# Revit family: VENTS-VKH
name_source: partatom
category: Mechanical Equipment
units: mm (PartAtom-declared; Revit-internal decimal feet)

## family parameters
Always vertical = Yes
Classification = None
Cut with Voids When Loaded = No
OmniClass Number = 23.75.35.17.14
OmniClass Title = Fans, Single Units
Part Type = Normal
Room Calculation Point = No
Round Connector Dimension = Use Diameter
Shared = No
Work Plane-Based = No

## types (38) — shared parameters
Casing Material = Fan Zinc
Description = Centrifugal roof fan with horizontal air discharge
Family Version = 1.0
Grid Material = Grid Cross Zinc
Hb = 30 mm  [stored 0.0984252 ft]
Load Classification = HVAC
Maintenance Zone Front Depth = 400 mm
Maintenance Zone Material = Maintenance Zone
Maintenance Zone Side Depth = 400 mm
Manufacturer = Vents
Power Factor = 1
Protection rating = IP X4
URL = https://ventilation-system.com
grGap1 = 1 mm  [stored 0.00328084 ft]
grGap2 = 20 mm  [stored 0.0656168 ft]
zero-valued in all types: Sound Pressure Level at 1 m (dBA), Sound Pressure Level at 3 m (dBA)

## per-type parameters (varying)
| type | A | Ac | Atop | B | C | Current | D | Duct Connection Size | H | Hc | Ht1 | Ht2 | Maximum Air Flow | Model | Noise Level at 3 m (dBa) | Number of Poles | RPM (min-1) | Transported Air Temperature (°C) | Type Comments | Voltage | Weight | gsA |
| VKH 2E 190 (50Hz) | 351 mm | 298 mm  [stored 0.97769 ft] | 294 mm  [stored 0.964567 ft] | 350 mm | 245 mm  [stored 0.803806 ft] | 0 A | 213 mm  [stored 0.698819 ft] | 180 mm  [stored 0.590551 ft] | 189 mm  [stored 0.620079 ft] | 78 mm | 59 mm | 22 mm  [stored 0.0721785 ft] | 610 m³/h | VKH 2E 190 | 48 | 1 | 2680 | -25...+50 | Centrifugal roof fan VKH 2E 190 | 230 V | 8.20 kg | 281 mm |
| VKH 2E 190 (60Hz) | 351 mm | 298 mm  [stored 0.97769 ft] | 294 mm  [stored 0.964567 ft] | 350 mm | 245 mm  [stored 0.803806 ft] | 0 A | 213 mm  [stored 0.698819 ft] | 180 mm  [stored 0.590551 ft] | 189 mm  [stored 0.620079 ft] | 78 mm | 59 mm | 22 mm  [stored 0.0721785 ft] | 654 m³/h | VKH 2E 190 | 49 | 1 | 2980 | -25...+50 | Centrifugal roof fan VKH 2E 190 | 230 V | 8.20 kg | 281 mm |
| VKH 2E 220 (50Hz) | 337 mm | 284 mm  [stored 0.931759 ft] | 292 mm  [stored 0.958005 ft] | 338 mm | 245 mm  [stored 0.803806 ft] | 0 A | 213 mm  [stored 0.698819 ft] | 180 mm  [stored 0.590551 ft] | 180 mm  [stored 0.590551 ft] | 75 mm | 46 mm  [stored 0.150919 ft] | 29 mm  [stored 0.0951444 ft] | 880 m³/h | VKH 2E 220 | 50 | 1 | 2580 | -25...+50 | Centrifugal roof fan VKH 2E 220 | 230 V | 7.00 kg | 270 mm |
| VKH 2E 220 (60Hz) | 337 mm | 284 mm  [stored 0.931759 ft] | 292 mm  [stored 0.958005 ft] | 338 mm | 245 mm  [stored 0.803806 ft] | 1 A | 213 mm  [stored 0.698819 ft] | 180 mm  [stored 0.590551 ft] | 180 mm  [stored 0.590551 ft] | 75 mm | 46 mm  [stored 0.150919 ft] | 29 mm  [stored 0.0951444 ft] | 883 m³/h | VKH 2E 220 | 51 | 1 | 2840 | -25...+50 | Centrifugal roof fan VKH 2E 220 | 230 V | 7.00 kg | 270 mm |
| VKH 2E 225 (50Hz) | 351 mm | 298 mm  [stored 0.97769 ft] | 295 mm  [stored 0.967848 ft] | 350 mm | 245 mm  [stored 0.803806 ft] | 1 A | 210 mm  [stored 0.688976 ft] | 180 mm  [stored 0.590551 ft] | 210 mm  [stored 0.688976 ft] | 99 mm | 59 mm | 22 mm  [stored 0.0721785 ft] | 915 m³/h | VKH 2E 225 | 51 | 1 | 2790 | -25...+50 | Centrifugal roof fan VKH 2E 225 | 230 V | 9.20 kg | 281 mm |
| VKH 2E 225 (60Hz) | 351 mm | 298 mm  [stored 0.97769 ft] | 295 mm  [stored 0.967848 ft] | 350 mm | 245 mm  [stored 0.803806 ft] | 1 A | 210 mm  [stored 0.688976 ft] | 180 mm  [stored 0.590551 ft] | 210 mm  [stored 0.688976 ft] | 99 mm | 59 mm | 22 mm  [stored 0.0721785 ft] | 1010 m³/h | VKH 2E 225 | 52 | 1 | 2820 | -25...+50 | Centrifugal roof fan VKH 2E 225 | 230 V | 9.20 kg | 281 mm |
| VKH 4E 225 (50Hz) | 351 mm | 298 mm  [stored 0.97769 ft] | 295 mm  [stored 0.967848 ft] | 350 mm | 245 mm  [stored 0.803806 ft] | 0 A | 210 mm  [stored 0.688976 ft] | 180 mm  [stored 0.590551 ft] | 233 mm  [stored 0.764436 ft] | 122 mm | 59 mm | 22 mm  [stored 0.0721785 ft] | 738 m³/h | VKH 4E 225 | 45 | 1 | 1400 | -25...+50 | Centrifugal roof fan VKH 4E 225 | 230 V | 8.80 kg | 281 mm |
| VKH 2E 250 (50Hz) | 451 mm | 398 mm | 394 mm | 450 mm | 330 mm | 1 A | 285 mm  [stored 0.935039 ft] | 250 mm  [stored 0.82021 ft] | 237 mm  [stored 0.777559 ft] | 126 mm  [stored 0.413386 ft] | 59 mm | 22 mm  [stored 0.0721785 ft] | 1450 m³/h | VKH 2E 250 | 54 | 1 | 2480 | -25...+50 | Centrifugal roof fan VKH 2E 250 | 230 V | 12.70 kg | 361 mm |
| VKH 2E 250 (60Hz) | 451 mm | 398 mm | 394 mm | 450 mm | 330 mm | 1 A | 285 mm  [stored 0.935039 ft] | 250 mm  [stored 0.82021 ft] | 237 mm  [stored 0.777559 ft] | 126 mm  [stored 0.413386 ft] | 59 mm | 22 mm  [stored 0.0721785 ft] | 1320 m³/h | VKH 2E 250 | 53 | 1 | 2320 | -25...+50 | Centrifugal roof fan VKH 2E 250 | 230 V | 12.70 kg | 361 mm |
| VKH 4E 250 (50Hz) | 451 mm | 398 mm | 394 mm | 450 mm | 330 mm | 0 A | 285 mm  [stored 0.935039 ft] | 250 mm  [stored 0.82021 ft] | 237 mm  [stored 0.777559 ft] | 126 mm  [stored 0.413386 ft] | 59 mm | 22 mm  [stored 0.0721785 ft] | 820 m³/h | VKH 4E 250 | 46 | 1 | 1440 | -25...+50 | Centrifugal roof fan VKH 4E 250 | 230 V | 12.10 kg | 361 mm |
| VKH 4E 280 (50Hz) | 451 mm | 398 mm | 394 mm | 450 mm | 330 mm | 1 A | 291 mm  [stored 0.954724 ft] | 250 mm  [stored 0.82021 ft] | 265 mm  [stored 0.869423 ft] | 154 mm | 59 mm | 22 mm  [stored 0.0721785 ft] | 1490 m³/h | VKH 4E 280 | 46 | 1 | 1446 | -25...+50 | Centrifugal roof fan VKH 4E 280 | 230 V | 13.50 kg | 361 mm |
| VKH 4E 280 (60Hz) | 451 mm | 398 mm | 394 mm | 450 mm | 330 mm | 1 A | 291 mm  [stored 0.954724 ft] | 250 mm  [stored 0.82021 ft] | 265 mm  [stored 0.869423 ft] | 154 mm | 59 mm | 22 mm  [stored 0.0721785 ft] | 1520 m³/h | VKH 4E 280 | 46 | 1 | 1710 | -25...+50 | Centrifugal roof fan VKH 4E 280 | 230 V | 13.50 kg | 361 mm |
| VKH 2E 310 (50Hz) | 451 mm | 398 mm | 394 mm | 450 mm | 330 mm | 1 A | 291 mm  [stored 0.954724 ft] | 250 mm  [stored 0.82021 ft] | 251 mm  [stored 0.823491 ft] | 140 mm  [stored 0.459318 ft] | 59 mm | 22 mm  [stored 0.0721785 ft] | 2150 m³/h | VKH 2E 310 | 58 | 1 | 2620 | -25...+50 | Centrifugal roof fan VKH 2E 310 | 230 V | 13.20 kg | 361 mm |
| VKH 4E 310 (50Hz) | 451 mm | 398 mm | 394 mm | 450 mm | 330 mm | 1 A | 285 mm  [stored 0.935039 ft] | 250 mm  [stored 0.82021 ft] | 287 mm  [stored 0.941601 ft] | 176 mm  [stored 0.577428 ft] | 59 mm | 22 mm  [stored 0.0721785 ft] | 2265 m³/h | VKH 4E 310 | 47 | 1 | 1420 | -25...+50 | Centrifugal roof fan VKH 4E 310 | 230 V | 14.20 kg | 361 mm |
| VKH 4E 310 (60Hz) | 451 mm | 398 mm | 394 mm | 450 mm | 330 mm | 1 A | 285 mm  [stored 0.935039 ft] | 250 mm  [stored 0.82021 ft] | 287 mm  [stored 0.941601 ft] | 176 mm  [stored 0.577428 ft] | 59 mm | 22 mm  [stored 0.0721785 ft] | 2425 m³/h | VKH 4E 310 | 49 | 1 | 1740 | -25...+50 | Centrifugal roof fan VKH 4E 310 | 230 V | 14.20 kg | 361 mm |
| VKH 4D 310 (50Hz) | 451 mm | 398 mm | 394 mm | 450 mm | 330 mm | 0 A | 285 mm  [stored 0.935039 ft] | 250 mm  [stored 0.82021 ft] | 287 mm  [stored 0.941601 ft] | 176 mm  [stored 0.577428 ft] | 59 mm | 22 mm  [stored 0.0721785 ft] | 2300 m³/h | VKH 4D 310 | 47 | 3 | 1410 | -25...+50 | Centrifugal roof fan VKH 4D 310 | 400 V | 14.20 kg | 361 mm |
| VKH 4D 310 (60Hz) | 451 mm | 398 mm | 394 mm | 450 mm | 330 mm | 0 A | 285 mm  [stored 0.935039 ft] | 250 mm  [stored 0.82021 ft] | 287 mm  [stored 0.941601 ft] | 176 mm  [stored 0.577428 ft] | 59 mm | 22 mm  [stored 0.0721785 ft] | 2442 m³/h | VKH 4D 310 | 48 | 3 | 1550 | -25...+50 | Centrifugal roof fan VKH 4D 310 | 400 V | 14.20 kg | 361 mm |
| VKH 4E 355 (50Hz) | 625 mm | 568 mm | 534 mm | 620 mm | 450 mm | 1 A | 438 mm | 400 mm | 322 mm | 176 mm  [stored 0.577428 ft] | 94 mm  [stored 0.308399 ft] | 22 mm  [stored 0.0721785 ft] | 2480 m³/h | VKH 4E 355 | 51 | 1 | 1420 | -30...+60 | Centrifugal roof fan VKH 4E 355 | 230 V | 28.30 kg | 500 mm |
| VKH 4E 355 (60Hz) | 625 mm | 568 mm | 534 mm | 620 mm | 450 mm | 1 A | 438 mm | 400 mm | 322 mm | 176 mm  [stored 0.577428 ft] | 94 mm  [stored 0.308399 ft] | 22 mm  [stored 0.0721785 ft] | 2976 m³/h | VKH 4E 355 | 52 | 1 | 1580 | -30...+60 | Centrifugal roof fan VKH 4E 355 | 230 V | 28.30 kg | 500 mm |
| VKH 4D 355 (50Hz) | 625 mm | 568 mm | 534 mm | 620 mm | 450 mm | 1 A | 438 mm | 400 mm | 347 mm | 201 mm  [stored 0.659449 ft] | 94 mm  [stored 0.308399 ft] | 22 mm  [stored 0.0721785 ft] | 3290 m³/h | VKH 4D 355 | 52 | 3 | 1430 | -30...+60 | Centrifugal roof fan VKH 4D 355 | 400 V | 30.30 kg | 500 mm |
| VKH 4D 355 (60Hz) | 625 mm | 568 mm | 534 mm | 620 mm | 450 mm | 1 A | 438 mm | 400 mm | 347 mm | 201 mm  [stored 0.659449 ft] | 94 mm  [stored 0.308399 ft] | 22 mm  [stored 0.0721785 ft] | 3540 m³/h | VKH 4D 355 | 53 | 3 | 1650 | -30...+60 | Centrifugal roof fan VKH 4D 355 | 400 V | 30.30 kg | 500 mm |
| VKH 4E 400 (50Hz) | 625 mm | 568 mm | 534 mm | 620 mm | 450 mm | 2 A | 438 mm | 400 mm | 376 mm | 230 mm | 94 mm  [stored 0.308399 ft] | 22 mm  [stored 0.0721785 ft] | 3950 m³/h | VKH 4E 400 | 55 | 1 | 1440 | -30...+60 | Centrifugal roof fan VKH 4E 400 | 230 V | 35.00 kg | 500 mm |
| VKH 6E 400 (50Hz) | 625 mm | 568 mm | 534 mm | 620 mm | 450 mm | 1 A | 438 mm | 400 mm | 376 mm | 230 mm | 94 mm  [stored 0.308399 ft] | 22 mm  [stored 0.0721785 ft] | 2740 m³/h | VKH 6E 400 | 47 | 1 | 945 | -30...+60 | Centrifugal roof fan VKH 6E 400 | 230 V | 32.70 kg | 500 mm |
| VKH 6E 400 (60Hz) | 625 mm | 568 mm | 534 mm | 620 mm | 450 mm | 1 A | 438 mm | 400 mm | 376 mm | 230 mm | 94 mm  [stored 0.308399 ft] | 22 mm  [stored 0.0721785 ft] | 3289 m³/h | VKH 6E 400 | 49 | 1 | 1071 | -30...+60 | Centrifugal roof fan VKH 6E 400 | 230 V | 32.70 kg | 500 mm |
| VKH 4D 400 (50Hz) | 625 mm | 568 mm | 534 mm | 620 mm | 450 mm | 1 A | 438 mm | 400 mm | 376 mm | 230 mm | 94 mm  [stored 0.308399 ft] | 22 mm  [stored 0.0721785 ft] | 3950 m³/h | VKH 4D 400 | 55 | 3 | 1440 | -30...+60 | Centrifugal roof fan VKH 4D 400 | 400 V | 35.00 kg | 500 mm |
| VKH 4E 450 (50Hz) | 710 mm | 624 mm | 600 mm | 700 mm | 535 mm | 3 A | 438 mm | 400 mm | 420 mm | 254 mm  [stored 0.833333 ft] | 114 mm  [stored 0.374016 ft] | 22 mm  [stored 0.0721785 ft] | 6180 m³/h | VKH 4E 450 | 58 | 1 | 1400 | -30...+60 | Centrifugal roof fan VKH 4E 450 | 230 V | 46.60 kg | 568 mm |
| VKH 6E 450 (50Hz) | 710 mm | 624 mm | 600 mm | 700 mm | 535 mm | 1 A | 438 mm | 400 mm | 420 mm | 254 mm  [stored 0.833333 ft] | 114 mm  [stored 0.374016 ft] | 22 mm  [stored 0.0721785 ft] | 4380 m³/h | VKH 6E 450 | 50 | 1 | 940 | -30...+60 | Centrifugal roof fan VKH 6E 450 | 230 V | 45.60 kg | 568 mm |
| VKH 4D 450 (50Hz) | 710 mm | 624 mm | 600 mm | 700 mm | 535 mm | 2 A | 438 mm | 400 mm | 420 mm | 254 mm  [stored 0.833333 ft] | 114 mm  [stored 0.374016 ft] | 22 mm  [stored 0.0721785 ft] | 5920 m³/h | VKH 4D 450 | 57 | 3 | 1440 | -30...+50 | Centrifugal roof fan VKH 4D 450 | 400 V | 45.50 kg | 568 mm |
| VKH 4D 500 (50Hz) | 710 mm | 624 mm | 600 mm | 700 mm | 535 mm | 3 A | 430 mm | 400 mm | 490 mm | 324 mm | 114 mm  [stored 0.374016 ft] | 22 mm  [stored 0.0721785 ft] | 8435 m³/h | VKH 4D 500 | 62 | 3 | 1460 | -30...+50 | Centrifugal roof fan VKH 4D 500 | 400 V | 46.60 kg | 568 mm |
| VKH 6E 500 (50Hz) | 710 mm | 624 mm | 600 mm | 700 mm | 535 mm | 2 A | 445 mm | 400 mm | 461 mm | 295 mm  [stored 0.967848 ft] | 114 mm  [stored 0.374016 ft] | 22 mm  [stored 0.0721785 ft] | 5680 m³/h | VKH 6E 500 | 52 | 1 | 970 | -25...+60 | Centrifugal roof fan VKH 6E 500 | 230 V | 52.80 kg | 568 mm |
| VKH 6E 500 (60Hz) | 710 mm | 624 mm | 600 mm | 700 mm | 535 mm | 3 A | 445 mm | 400 mm | 461 mm | 295 mm  [stored 0.967848 ft] | 114 mm  [stored 0.374016 ft] | 22 mm  [stored 0.0721785 ft] | 6532 m³/h | VKH 6E 500 | 54 | 1 | 1120 | -25...+60 | Centrifugal roof fan VKH 6E 500 | 230 V | 52.80 kg | 568 mm |
| VKH 6D 500 (50Hz) | 710 mm | 624 mm | 600 mm | 700 mm | 535 mm | 1 A | 445 mm | 400 mm | 461 mm | 295 mm  [stored 0.967848 ft] | 114 mm  [stored 0.374016 ft] | 22 mm  [stored 0.0721785 ft] | 6000 m³/h | VKH 6D 500 | 52 | 3 | 978 | -25...+60 | Centrifugal roof fan VKH 6D 500 | 400 V | 52.70 kg | 568 mm |
| VKH 6D 500 (60Hz) | 710 mm | 624 mm | 600 mm | 700 mm | 535 mm | 1 A | 445 mm | 400 mm | 461 mm | 295 mm  [stored 0.967848 ft] | 114 mm  [stored 0.374016 ft] | 22 mm  [stored 0.0721785 ft] | 6122 m³/h | VKH 6D 500 | 54 | 3 | 1125 | -25...+60 | Centrifugal roof fan VKH 6D 500 | 400 V | 52.70 kg | 568 mm |
| VKH 4D 560 (50Hz) | 900 mm | 838 mm | 790 mm | 895 mm | 750 mm | 3 A | 605 mm | 560 mm | 489 mm | 323 mm | 114 mm  [stored 0.374016 ft] | 22 mm  [stored 0.0721785 ft] | 13560 m³/h | VKH 4D 560 | 66 | 1 | 1400 | -25...+50 | Centrifugal roof fan VKH 4D 560 | 230 V | 81.40 kg | 720 mm |
| VKH 6E 560 (50Hz) | 900 mm | 838 mm | 790 mm | 895 mm | 750 mm | 3 A | 605 mm | 560 mm | 489 mm | 323 mm | 114 mm  [stored 0.374016 ft] | 22 mm  [stored 0.0721785 ft] | 9560 m³/h | VKH 6E 560 | 58 | 1 | 930 | -25...+50 | Centrifugal roof fan VKH 6E 560 | 230 V | 76.40 kg | 720 mm |
| VKH 6D 560 (50Hz) | 900 mm | 838 mm | 790 mm | 895 mm | 750 mm | 1 A | 605 mm | 560 mm | 489 mm | 323 mm | 114 mm  [stored 0.374016 ft] | 22 mm  [stored 0.0721785 ft] | 9630 m³/h | VKH 6D 560 | 58 | 3 | 970 | -25...+50 | Centrifugal roof fan VKH 6D 560 | 400 V | 76.40 kg | 720 mm |
| VKH 6D 630 (50Hz) | 1000 mm | 915 mm | 892 mm | 990 mm | 750 mm | 2 A | 600 mm | 560 mm | 520 mm | 354 mm | 114 mm  [stored 0.374016 ft] | 22 mm  [stored 0.0721785 ft] | 12640 m³/h | VKH 6D 630 | 64 | 3 | 957 | -25...+50 | Centrifugal roof fan VKH 6D 630 | 400 V | 96.30 kg | 800 mm |
| VKH 6D 710 (50Hz) | 1060 mm | 975 mm | 950 mm | 1050 mm | 840 mm | 5 A | 674 mm | 630 mm | 570 mm | 404 mm | 114 mm  [stored 0.374016 ft] | 22 mm  [stored 0.0721785 ft] | 17010 m³/h | VKH 6D 710 | 67 | 3 | 945 | -25...+70 | Centrifugal roof fan VKH 6D 710 | 400 V | 134.00 kg | 848 mm |

note: [stored X ft] marks values corroborated as IEEE doubles in the binary element streams (Revit-internal decimal feet)

## geometry (parser evidence)
native form markers: Sweep x5
no freeform markers — native parametric forms only
